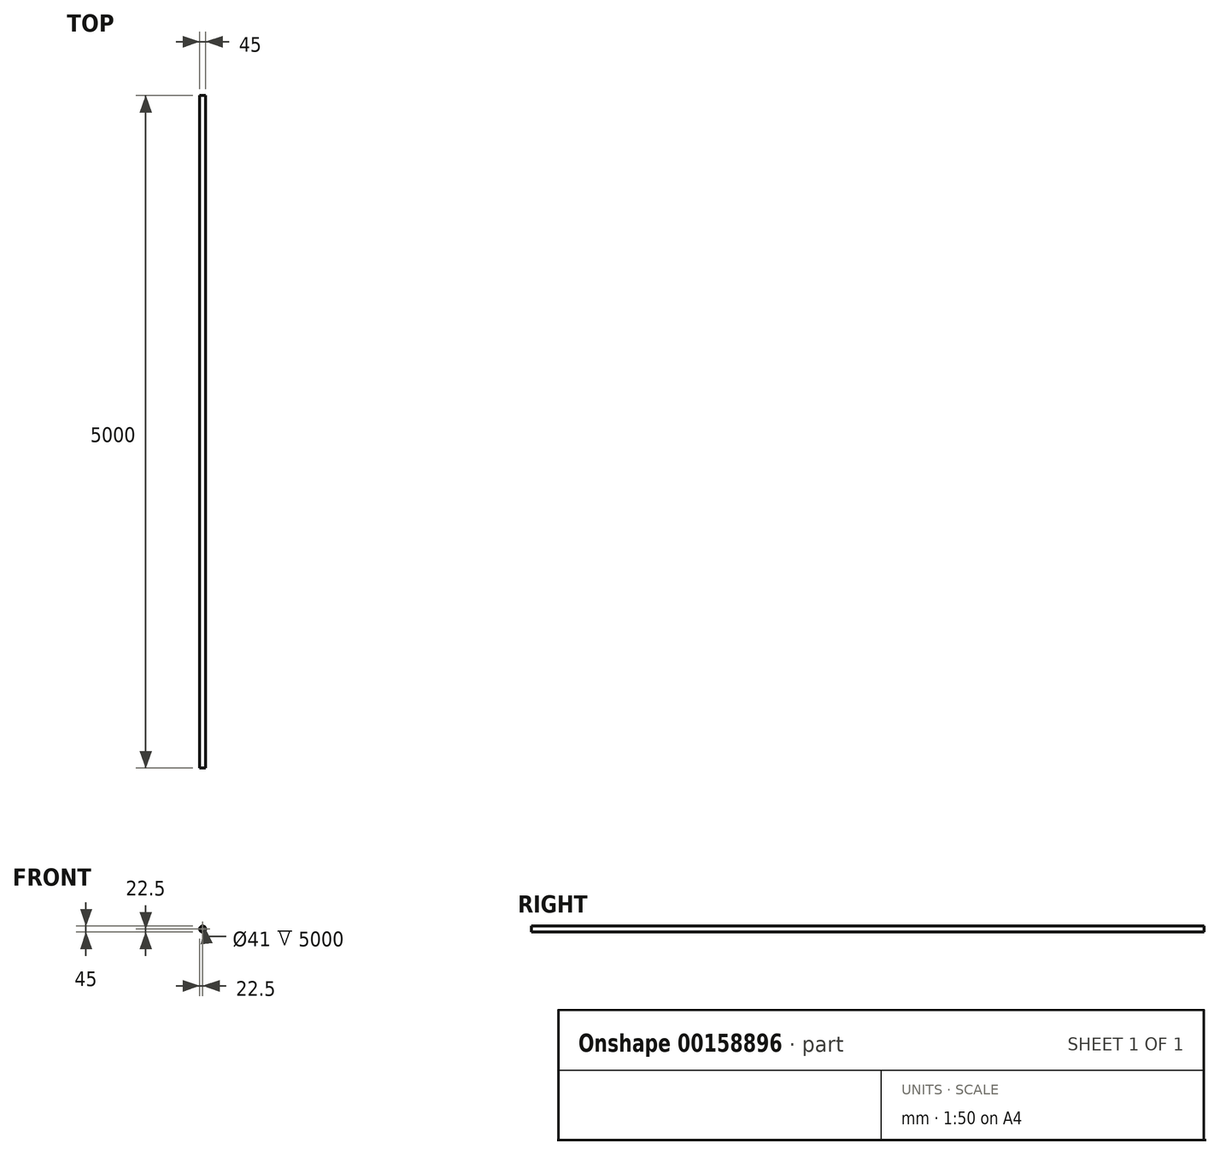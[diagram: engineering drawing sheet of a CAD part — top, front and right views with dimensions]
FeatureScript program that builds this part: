
annotation { "Feature Type Name" : "Feature", "Feature Type Description" : "" }
export const myFeature = defineFeature(function(context is Context, id is Id, definition is map)
    precondition{}
    {
        {
            var Q0;
            Q0=qCreatedBy(makeId("Front.planeOp"),FACE);
            var sketch = newSketch(context, id + "F0", { "sketchPlane" : qUnion([Q0])});
            skCircle(sketch, "E0", {"center": v(0, 0) * mm, "radius": 22.5 * mm});
            skCircle(sketch, "E1.0", {"center": v(0, 0) * mm, "radius": 20.5 * mm});
            skSolve(sketch);
        }
        {
            var Q0;
            Q0=makeQuery(id+"F0.imprint","IMPRINT",FACE,{"disambiguationData":[TD([[makeQuery(id+"F0.imprint","IMPRINT",EDGE,{"derivedFrom":sQuery(id+"F0.wireOp",EDGE,"E0")}),1.0]])]});
            extrude(context, id + "F1", {"entities" : qUnion([Q0]), "depth" : 5000 * mm});
        }
    });
